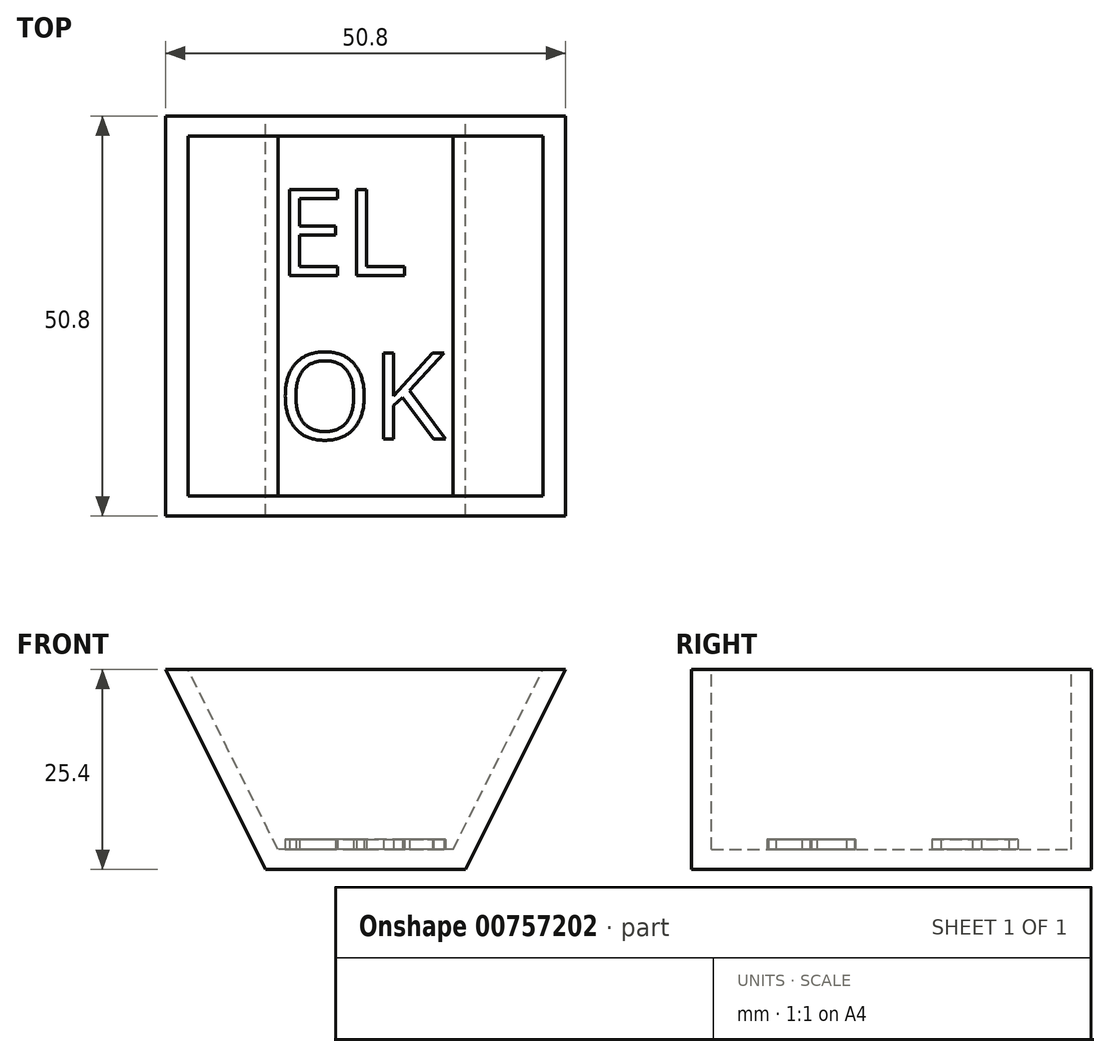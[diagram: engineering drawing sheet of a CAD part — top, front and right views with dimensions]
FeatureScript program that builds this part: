
annotation { "Feature Type Name" : "Feature", "Feature Type Description" : "" }
export const myFeature = defineFeature(function(context is Context, id is Id, definition is map)
    precondition{}
    {
        {
            var Q0;
            Q0=qCreatedBy(makeId("Front.planeOp"),FACE);
            var sketch = newSketch(context, id + "F0", { "sketchPlane" : qUnion([Q0])});
            skLineSegment(sketch, "E0", {"start": v(-54.22, 22.87) * mm, "end": v(-3.42, 22.87) * mm});
            skPoint(sketch, "E1.start.orphan", {"position": v(-52.42, 0) * mm});
            skPoint(sketch, "E2.end.orphan", {"position": v(-16.12, 0) * mm});
            skLineSegment(sketch, "E3", {"start": v(-28.82, 22.87) * mm, "end": v(-28.82, -2.53) * mm});
            skPoint(sketch, "E4.start.orphan", {"position": v(-45.33, -2.53) * mm});
            skLineSegment(sketch, "E5", {"start": v(-28.82, -2.53) * mm, "end": v(-41.52, -2.53) * mm});
            skLineSegment(sketch, "E6", {"start": v(-28.82, -2.53) * mm, "end": v(-16.12, -2.53) * mm});
            skLineSegment(sketch, "E7", {"start": v(-41.52, -2.53) * mm, "end": v(-54.22, 22.87) * mm});
            skLineSegment(sketch, "E8", {"start": v(-16.12, -2.53) * mm, "end": v(-3.42, 22.87) * mm});
            skSolve(sketch);
        }
        {
            var Q0;
            {var subQ2=sQuery(id+"F0.wireOp",EDGE,"E3");Q0=makeQuery(id+"F0.imprint","IMPRINT",FACE,{"disambiguationData":[TD([[makeQuery(id+"F0.imprint","IMPRINT",EDGE,{"derivedFrom":subQ2}),-1.0]])]});}
            var Q1;
            {var subQ2=sQuery(id+"F0.wireOp",EDGE,"E3");Q1=makeQuery(id+"F0.imprint","IMPRINT",FACE,{"disambiguationData":[TD([[makeQuery(id+"F0.imprint","IMPRINT",EDGE,{"derivedFrom":subQ2}),1.0]])]});}
            extrude(context, id + "F1", {"entities" : qUnion([Q0, Q1]), "depth" : 50.8 * mm, "offsetDistance" : 25.4 * mm});
        }
        {
            var Q0;
            Q0=makeQuery(id+"F1.opExtrude","SWEPT_FACE",FACE,{"disambiguationData":[OSD([sQuery(id+"F0.wireOp",EDGE,"E0")])]});
            shell(context, id + "F2", {"entities" : qUnion([Q0]), "thickness" : 2.54 * mm});
        }
        {
            var Q0;
            Q0=makeQuery(id+"F2.opShell","OFFSET_FACE",FACE,{"disambiguationData":[OSD([sQuery(id+"F0.wireOp",EDGE,"E5"),sQuery(id+"F0.wireOp",EDGE,"E6")])]});
            var sketch = newSketch(context, id + "F3", { "sketchPlane" : qUnion([Q0])});
            skText(sketch, "E9", { "text": "EL\nOK", "fontName": "OpenSans-Regular.ttf"});
            const initialGuessF3  = {"E9": [-0.03995, -0.02026, 1, 0, 0.011]};
            skSetInitialGuess(sketch, initialGuessF3);
            skSolve(sketch);
        }
        {
            var Q0;
            Q0 = qSketchRegion(id + "F3", true);
            extrude(context, id + "F4", {"entities" : qUnion([Q0]), "operationType" : NewBodyOperationType.ADD, "depth" : 1.27 * mm, "offsetDistance" : 25.4 * mm});
        }
    });
